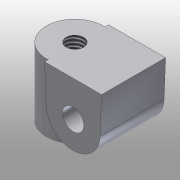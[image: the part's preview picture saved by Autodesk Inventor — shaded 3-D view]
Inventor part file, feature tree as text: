
AUTODESK INVENTOR PART (.ipt)
format: ipt  version: 2016 (Build 200138000, 138)  size: 116,736 bytes
history: native  units: mm
features: extrude x2, hole x2, sketch x2
ambient origin geometry x8: Origin, YZ Plane, XZ Plane, XY Plane, X Axis, Y Axis, Z Axis, Center Point
bodies: Solid1 (feature_tree)
feature tree (6):
  extrude  "Extrusion1"  Depth=5.0mm
  extrude  "Extrusion2"  Depth=9.0mm TaperAngle=0.0deg
  hole  "Hole2"  [1 undecoded]
  hole  "Hole3"  [1 undecoded]
  sketch  "Sketch1"  dims[d0=3.8mm d1=5.0mm]
  sketch  "Sketch2"  dims[d2=8.0mm d3=9.0mm d4=0.0mm d5=8.0mm d6=4.25mm d7=9.5mm d8=0.0mm d18=10.0mm d19=10.0mm d20=2.459mm d21=6.0mm d22=4.0mm d23=2.0mm d24=90.0deg d25=12.05mm d26=0.0mm d27=10.0mm d28=10.0mm d29=3.0mm d30=6.0mm d31=4.0mm d32=2.0mm d33=90.0deg d34=6.0mm d35=0.0mm]
note: 2 required parameter values undecoded (feature->parameter linkage not recoverable at this tier; creation-order binding heuristic only, values carry confidence <= 0.55)
